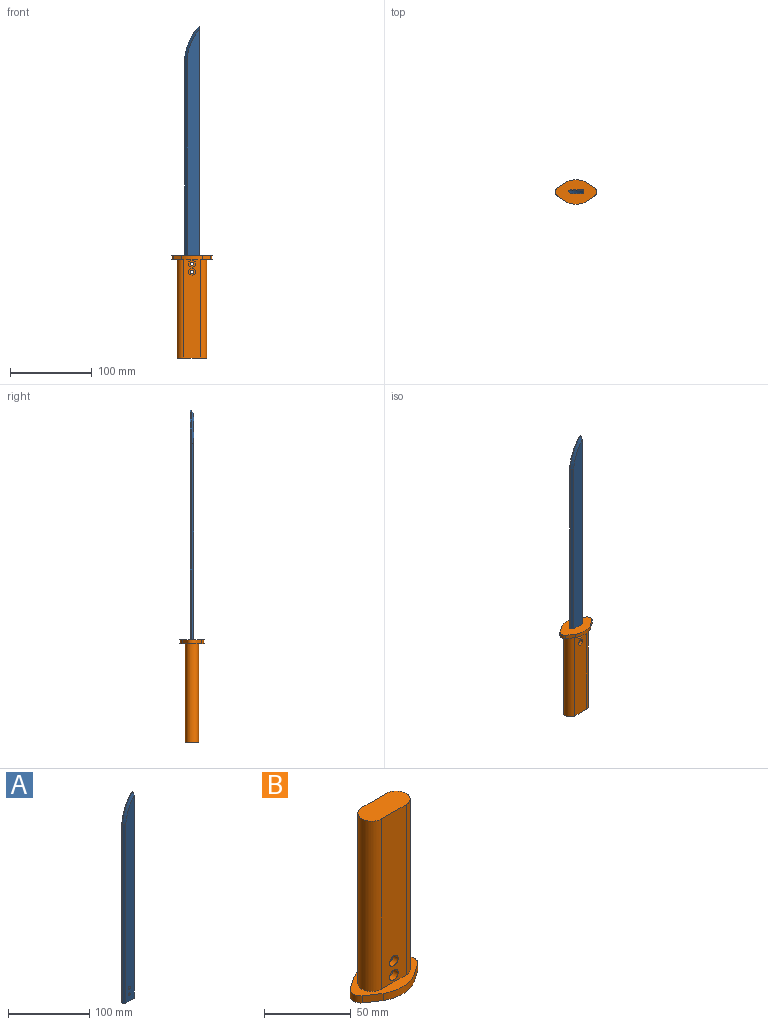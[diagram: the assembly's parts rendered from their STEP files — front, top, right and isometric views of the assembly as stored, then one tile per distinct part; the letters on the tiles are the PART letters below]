
ASSEMBLY  parts=2 mates=1
PART A: 10 faces, bbox 20.2x4x310 mm
  f0: plane 268.72x1mm, normal (-1,0,0), area 268.7mm2, adj f1,f4,f5,f7
  f1: plane 310x18mm, normal (0,1,0), area 5302.1mm2, adj f0,f3,f4,f5,f8,f9
  f2: plane 305.51x15mm, normal (0,-1,0), area 4366.3mm2, adj f3,f4,f6,f7,f8,f9
  f3: plane 310x4mm, normal (1,0,0), area 1233.3mm2, adj f1,f2,f4,f5,f6
  f4: plane 18x4mm, normal (0,0,-1), area 67.5mm2, adj f0,f1,f2,f3,f7
  f5: cylinder r=66.47mm len=41.28mm, axis (0,-1,0), area 45.9mm2, adj f0,f1,f3,f6
  f6: cone r=63.47mm half-angle=45deg, axis (0,1,0), area 183.4mm2, adj f2,f3,f5,f7
  f7: plane 268.73x3mm, normal (-0.71,-0.71,0), area 1139.9mm2, adj f0,f2,f4,f6
  f8: cylinder r=2mm len=4mm, axis (0,1,0), area 50.3mm2, adj f1,f2
  f9: cylinder r=2mm len=4mm, axis (0,1,0), area 50.3mm2, adj f1,f2
PART B: 43 faces, bbox 50x30x125 mm
  f0: cylinder r=2mm len=4mm, axis (0,-1,0), area 23.9mm2, adj f12,f32
  f1: cylinder r=2mm len=4mm, axis (0,-1,0), area 23.9mm2, adj f12,f30
  f2: plane 120x20mm, normal (0,1,0), area 2302.6mm2, adj f5,f7,f8,f15,f16,f17,f18,f19
  f3: cylinder r=2mm len=4mm, axis (0,-1,0), area 36.4mm2, adj f10,f28
  f4: cylinder r=2mm len=4mm, axis (0,-1,0), area 36.4mm2, adj f10,f21
  f5: cylinder r=8mm len=120mm, axis (0,0,-1), area 3015.9mm2, adj f2,f6,f8,f42
  f6: plane 120x20mm, normal (0,-1,0), area 2323mm2, adj f5,f7,f8,f29,f31,f42
  f7: cylinder r=8mm len=120mm, axis (0,0,-1), area 3015.9mm2, adj f2,f6,f8,f42
  f8: plane 36x16mm, normal (0,0,1), area 521.1mm2, adj f2,f5,f6,f7
  f9: plane 30x3mm, normal (0.71,-0.71,0), area 127.3mm2, adj f10,f13,f14,f41
  f10: plane 30x15.2mm, normal (0,-1,0), area 430.9mm2, adj f3,f4,f9,f11,f14,f41
  f11: plane 30x4.2mm, normal (-1,0,0), area 126mm2, adj f10,f12,f14,f41
  f12: plane 30x18.2mm, normal (0,1,0), area 520.9mm2, adj f0,f1,f11,f13,f14,f41
  f13: plane 30x1.2mm, normal (1,0,0), area 36mm2, adj f9,f12,f14,f41
  f14: plane 18.2x4.2mm, normal (0,0,-1), area 71.9mm2, adj f9,f10,f11,f12,f13
  f15: plane 4.33x3mm, normal (-1,0,0), area 13mm2, adj f2,f16,f20,f21
  f16: plane 3.75x3mm, normal (-0.5,0,0.87), area 13mm2, adj f2,f15,f17,f21
  f17: plane 3.75x3mm, normal (0.5,0,0.87), area 13mm2, adj f2,f16,f18,f21
  f18: plane 4.33x3mm, normal (1,0,0), area 13mm2, adj f2,f17,f19,f21
  f19: plane 3.75x3mm, normal (0.5,0,-0.87), area 13mm2, adj f2,f18,f20,f21
  f20: plane 3.75x3mm, normal (-0.5,0,-0.87), area 13mm2, adj f2,f15,f19,f21
  f21: plane 8.66x7.5mm, normal (0,1,0), area 36.1mm2, adj f4,f15,f16,f17,f18,f19,f20
  f22: plane 4.33x3mm, normal (-1,0,0), area 13mm2, adj f2,f23,f27,f28
  f23: plane 3.75x3mm, normal (-0.5,0,0.87), area 13mm2, adj f2,f22,f24,f28
  f24: plane 3.75x3mm, normal (0.5,0,0.87), area 13mm2, adj f2,f23,f25,f28
  f25: plane 4.33x3mm, normal (1,0,0), area 13mm2, adj f2,f24,f26,f28
  f26: plane 3.75x3mm, normal (0.5,0,-0.87), area 13mm2, adj f2,f25,f27,f28
  f27: plane 3.75x3mm, normal (-0.5,0,-0.87), area 13mm2, adj f2,f22,f26,f28
  f28: plane 8.66x7.5mm, normal (0,1,0), area 36.1mm2, adj f3,f22,f23,f24,f25,f26,f27
  f29: cylinder r=3.5mm len=7mm, axis (0,-1,0), area 88mm2, adj f6,f30
  f30: plane 7x7mm, normal (0,-1,0), area 25.9mm2, adj f1,f29
  f31: cylinder r=3.5mm len=7mm, axis (0,-1,0), area 88mm2, adj f6,f32
  f32: plane 7x7mm, normal (0,-1,0), area 25.9mm2, adj f0,f31
  f33: plane 10.2x6.8mm, normal (0.55,-0.83,0), area 61.3mm2, adj f34,f40,f41,f42
  f34: cylinder r=25.12mm len=24.96mm, axis (0,0,1), area 130.6mm2, adj f33,f35,f41,f42
  f35: plane 10.2x6.8mm, normal (-0.55,-0.83,0), area 61.3mm2, adj f34,f36,f41,f42
  f36: cylinder r=6.29mm len=9.76mm, axis (0,0,1), area 55.8mm2, adj f35,f37,f41,f42
  f37: plane 10.2x6.8mm, normal (-0.55,0.83,0), area 61.3mm2, adj f36,f38,f41,f42
  f38: cylinder r=25.12mm len=24.96mm, axis (0,0,1), area 130.6mm2, adj f37,f39,f41,f42
  f39: plane 10.2x6.8mm, normal (0.55,0.83,0), area 61.3mm2, adj f38,f40,f41,f42
  f40: cylinder r=6.29mm len=9.76mm, axis (0,0,1), area 55.8mm2, adj f33,f39,f41,f42
  f41: plane 50x30mm, normal (0,0,-1), area 992.5mm2, adj f9,f10,f11,f12,f13,f33,f34,f35
  f42: plane 50x30mm, normal (0,0,1), area 543.4mm2, adj f2,f5,f6,f7,f33,f34,f35,f36
PLACE A rot(axis=(-1,0,0),0deg) t=(-0.03,0,-123)mm
PLACE B rot(axis=(1,0,0),180deg) t=(0,0,-98)mm
MATE fastened A.f4 <-> B.f14  axis (0,0,-1) through (0.51,0.07,-123)mm
